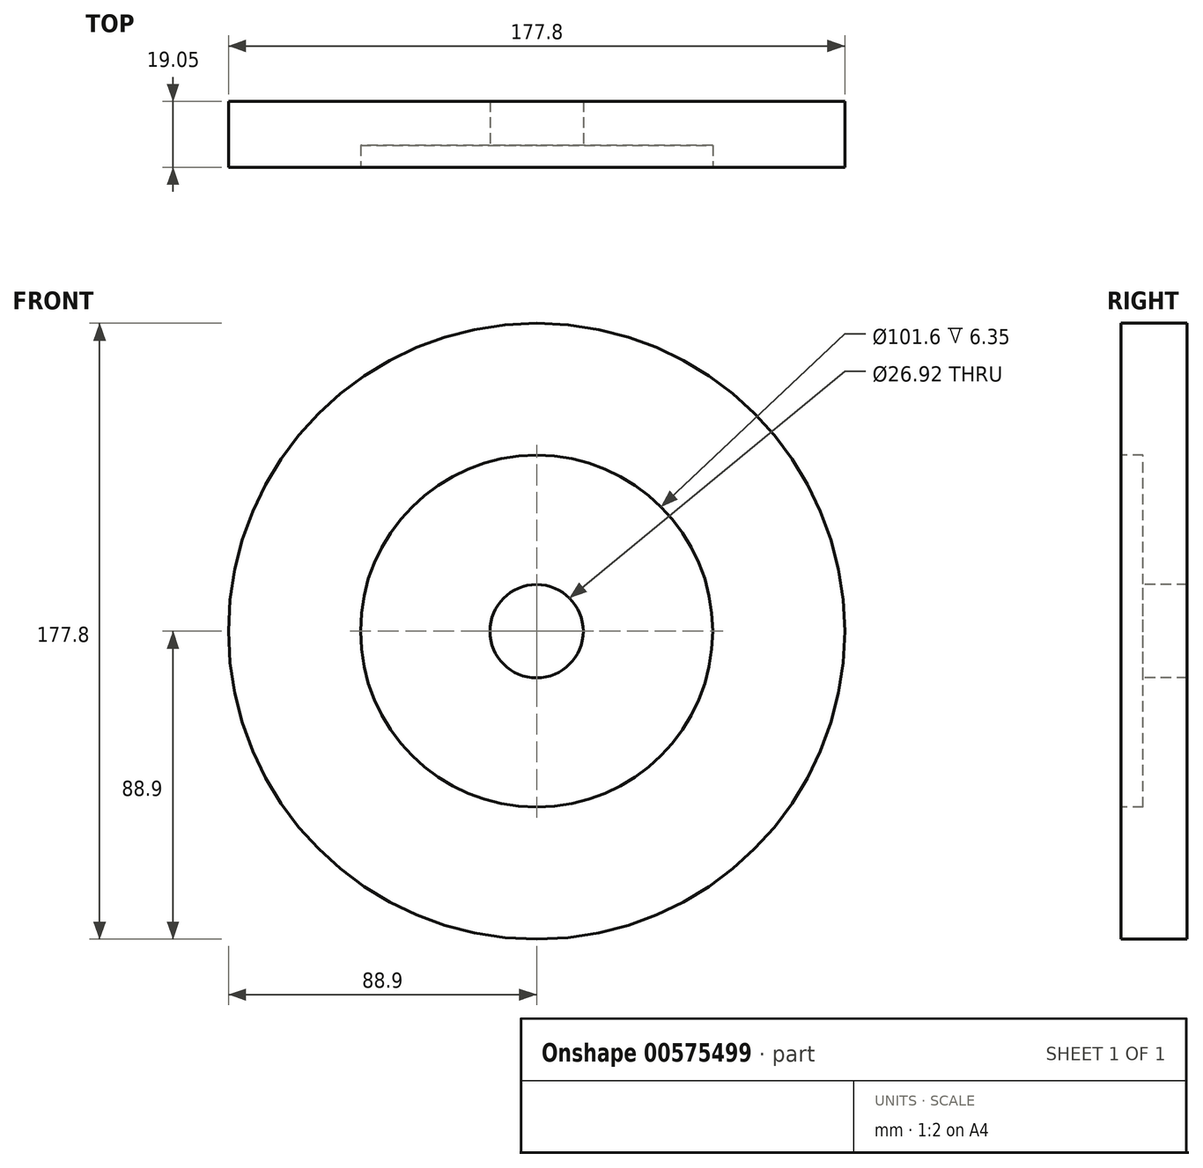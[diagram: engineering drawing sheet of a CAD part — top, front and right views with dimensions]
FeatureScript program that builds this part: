
annotation { "Feature Type Name" : "Feature", "Feature Type Description" : "" }
export const myFeature = defineFeature(function(context is Context, id is Id, definition is map)
    precondition{}
    {
        {
            var Q0;
            Q0=qCreatedBy(makeId("Front.planeOp"),FACE);
            var sketch = newSketch(context, id + "F0", { "sketchPlane" : qUnion([Q0])});
            skCircle(sketch, "E0", {"center": v(0, 0) * mm, "radius": 88.9 * mm});
            skSolve(sketch);
        }
        {
            var Q0;
            Q0 = qSketchRegion(id + "F0", true);
            extrude(context, id + "F1", {"entities" : qUnion([Q0]), "depth" : 19.05 * mm, "offsetDistance" : 25.4 * mm});
        }
        {
            var Q0;
            Q0=makeQuery(id+"F1.opExtrude","CAP_FACE",FACE,{"disambiguationData":[OSD([sQuery(id+"F0.wireOp",EDGE,"E0")])],"isStart":false});
            var sketch = newSketch(context, id + "F2", { "sketchPlane" : qUnion([Q0])});
            skCircle(sketch, "E1", {"center": v(0, 0) * mm, "radius": 50.8 * mm});
            skSolve(sketch);
        }
        {
            var Q0;
            Q0 = qSketchRegion(id + "F2", true);
            extrude(context, id + "F3", {"entities" : qUnion([Q0]), "operationType" : NewBodyOperationType.REMOVE, "oppositeDirection" : true, "depth" : 6.35 * mm, "offsetDistance" : 25.4 * mm});
        }
        {
            var Q0;
            Q0=makeQuery(id+"F3.boolean.opBoolean","COPY",FACE,{"derivedFrom":makeQuery(id+"F3.opExtrude","CAP_FACE",FACE,{"disambiguationData":[OSD([sQuery(id+"F2.wireOp",EDGE,"E1")])],"isStart":false})});
            var sketch = newSketch(context, id + "F4", { "sketchPlane" : qUnion([Q0])});
            skCircle(sketch, "E2", {"center": v(0, 0) * mm, "radius": 13.46 * mm});
            skSolve(sketch);
        }
        {
            var Q0;
            Q0=makeQuery(id+"F4.imprint","IMPRINT",FACE,{"disambiguationData":[TD([[makeQuery(id+"F4.imprint","IMPRINT",EDGE,{"derivedFrom":sQuery(id+"F4.wireOp",EDGE,"E2")}),1.0]])]});
            extrude(context, id + "F5", {"entities" : qUnion([Q0]), "operationType" : NewBodyOperationType.REMOVE, "oppositeDirection" : true, "depth" : 25.4 * mm, "offsetDistance" : 25.4 * mm});
        }
    });
